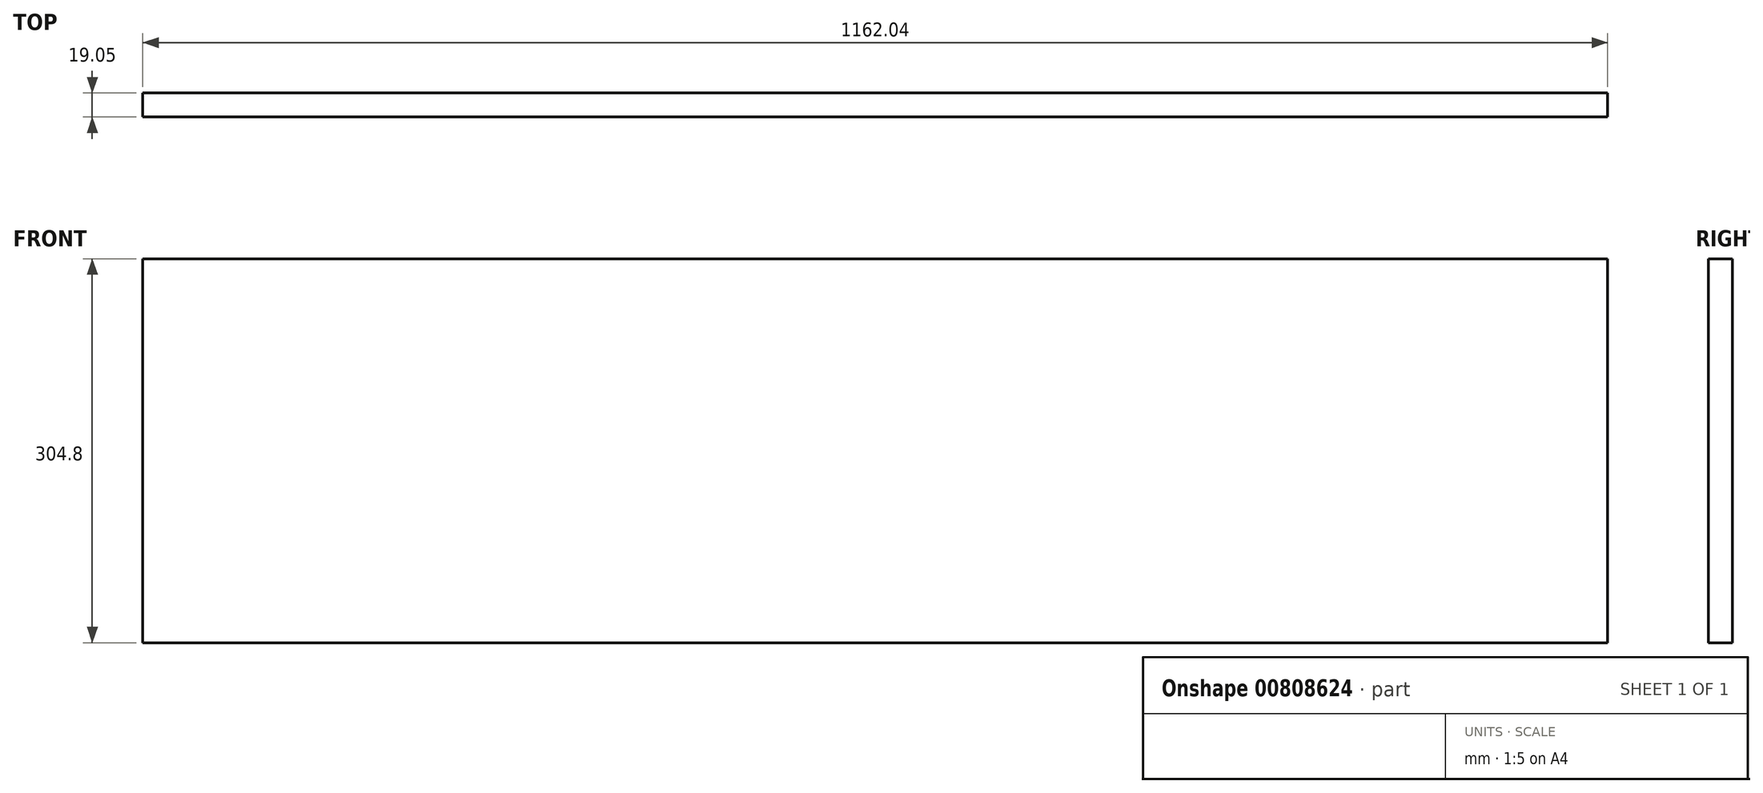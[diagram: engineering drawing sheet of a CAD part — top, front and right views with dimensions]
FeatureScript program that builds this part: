
annotation { "Feature Type Name" : "Feature", "Feature Type Description" : "" }
export const myFeature = defineFeature(function(context is Context, id is Id, definition is map)
    precondition{}
    {
        {
            var Q0;
            Q0=qCreatedBy(makeId("Front.planeOp"),FACE);
            var sketch = newSketch(context, id + "F0", { "sketchPlane" : qUnion([Q0])});
            skLineSegment(sketch, "E0.bottom", {"start": v(-581.02, 152.4) * mm, "end": v(581.02, 152.4) * mm});
            skLineSegment(sketch, "E0.top", {"start": v(-581.02, -152.4) * mm, "end": v(581.02, -152.4) * mm});
            skLineSegment(sketch, "E0.left", {"start": v(-581.02, 152.4) * mm, "end": v(-581.02, -152.4) * mm});
            skLineSegment(sketch, "E0.right", {"start": v(581.02, 152.4) * mm, "end": v(581.02, -152.4) * mm});
            skPoint(sketch, "E0.middle", {"position": v(0, 0) * mm});
            skSolve(sketch);
        }
        {
            var Q0;
            Q0=makeQuery(id+"F0.imprint","IMPRINT",FACE,{"disambiguationData":[TD([[makeQuery(id+"F0.imprint","IMPRINT",EDGE,{"derivedFrom":sQuery(id+"F0.wireOp",EDGE,"E0.bottom")}),-1.0]])]});
            extrude(context, id + "F1", {"entities" : qUnion([Q0]), "depth" : 19.05 * mm, "offsetDistance" : 25.4 * mm});
        }
    });
